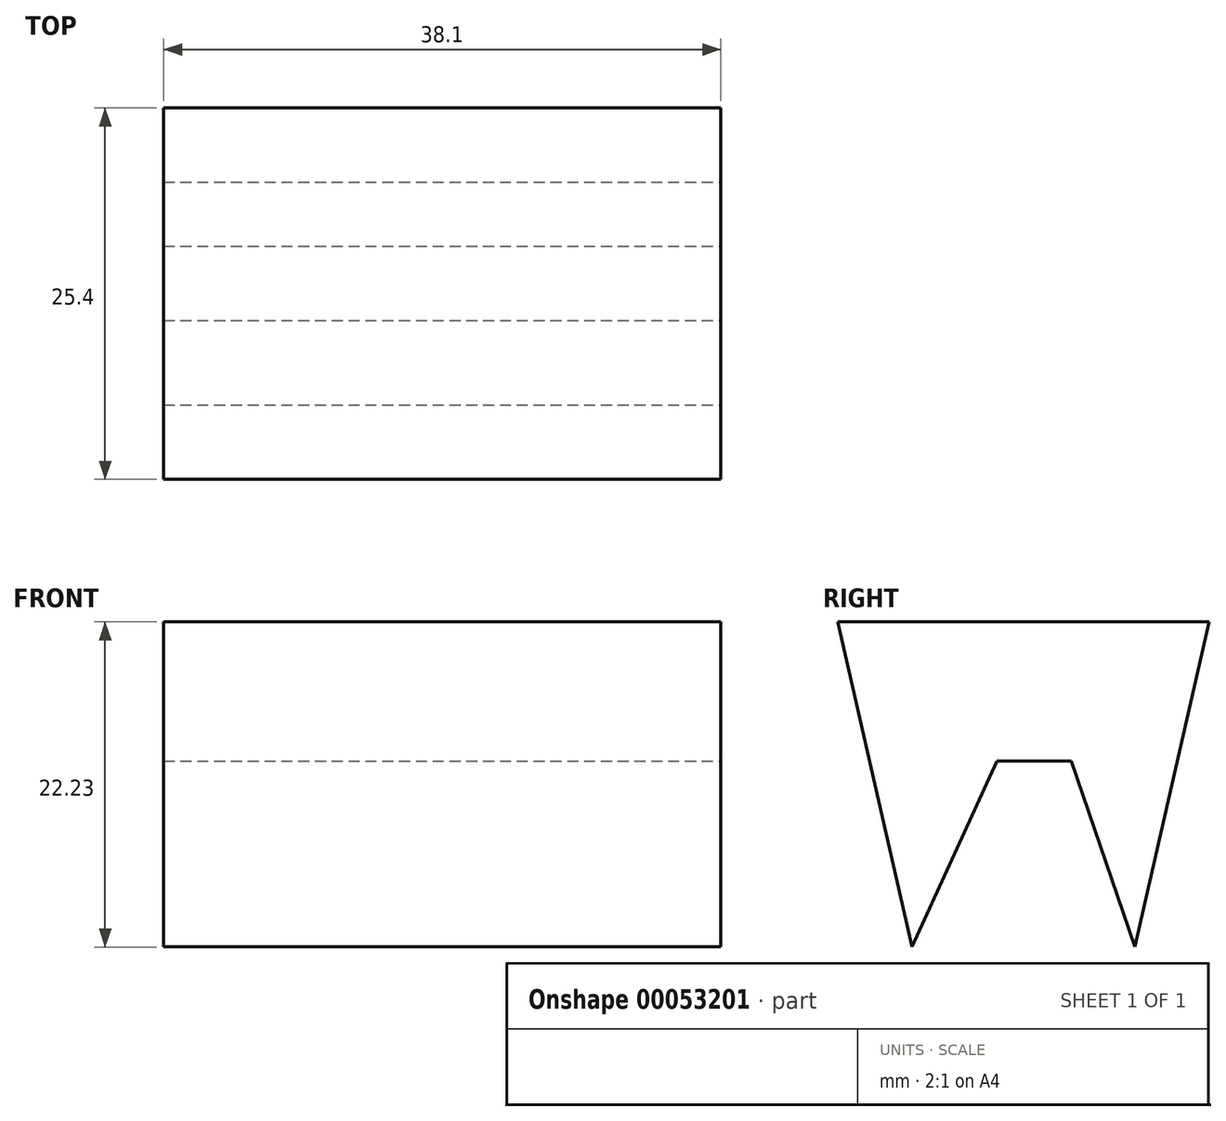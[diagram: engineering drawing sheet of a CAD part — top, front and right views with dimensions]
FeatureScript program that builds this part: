
annotation { "Feature Type Name" : "Feature", "Feature Type Description" : "" }
export const myFeature = defineFeature(function(context is Context, id is Id, definition is map)
    precondition{}
    {
        {
            var Q0;
            Q0=qCreatedBy(makeId("Front.planeOp"),FACE);
            var sketch = newSketch(context, id + "F0", { "sketchPlane" : qUnion([Q0])});
            skLineSegment(sketch, "E0.bottom", {"start": v(0, 0) * mm, "end": v(38.1, 0) * mm});
            skLineSegment(sketch, "E0.top", {"start": v(0, 38.1) * mm, "end": v(38.1, 38.1) * mm});
            skLineSegment(sketch, "E0.left", {"start": v(0, 0) * mm, "end": v(0, 38.1) * mm});
            skLineSegment(sketch, "E0.right", {"start": v(38.1, 0) * mm, "end": v(38.1, 38.1) * mm});
            skSolve(sketch);
        }
        {
            var Q0;
            Q0=makeQuery(id+"F0.imprint","IMPRINT",FACE,{"disambiguationData":[TD([[makeQuery(id+"F0.imprint","IMPRINT",EDGE,{"derivedFrom":sQuery(id+"F0.wireOp",EDGE,"E0.bottom")}),1.0]])]});
            extrude(context, id + "F1", {"entities" : qUnion([Q0]), "depth" : 38.1 * mm});
        }
        {
            var Q0;
            Q0=qCreatedBy(makeId("Front.planeOp"),FACE);
            cPlane(context, id + "F2", {"entities" : qUnion([Q0]), "cplaneType" : CPlaneType.OFFSET, "offset" : 38.1 * mm, "width" : 152.4 * mm, "height" : 152.4 * mm});
        }
        {
            var Q0;
            Q0=qCreatedBy(makeId("Right.planeOp"),FACE);
            cPlane(context, id + "F3", {"entities" : qUnion([Q0]), "cplaneType" : CPlaneType.OFFSET, "offset" : 38.1 * mm, "width" : 152.4 * mm, "height" : 152.4 * mm});
        }
        {
            var Q0;
            Q0=qCreatedBy(id+"F3.planeOp",FACE);
            var sketch = newSketch(context, id + "F4", { "sketchPlane" : qUnion([Q0])});
            skLineSegment(sketch, "E1", {"start": v(0, 0) * mm, "end": v(0, 38.1) * mm});
            skLineSegment(sketch, "E2", {"start": v(0, 38.1) * mm, "end": v(-38.1, 38.1) * mm});
            skLineSegment(sketch, "E3", {"start": v(-38.1, 38.1) * mm, "end": v(-38.1, 0) * mm});
            skLineSegment(sketch, "E4", {"start": v(-38.1, 38.1) * mm, "end": v(-31.75, 0) * mm});
            skLineSegment(sketch, "E5", {"start": v(-31.75, 0) * mm, "end": v(-25.4, 0) * mm});
            skLineSegment(sketch, "E6", {"start": v(-12.7, 0) * mm, "end": v(-6.35, 0) * mm});
            skLineSegment(sketch, "E7", {"start": v(-6.35, 0) * mm, "end": v(0, 38.1) * mm});
            skLineSegment(sketch, "E8", {"start": v(0, 38.1) * mm, "end": v(-6.35, 38.1) * mm});
            skLineSegment(sketch, "E9", {"start": v(-31.75, 38.1) * mm, "end": v(-38.1, 38.1) * mm});
            skLineSegment(sketch, "E10", {"start": v(-31.75, 38.1) * mm, "end": v(-26.67, 15.88) * mm});
            skLineSegment(sketch, "E11", {"start": v(-26.67, 15.88) * mm, "end": v(-20.87, 28.58) * mm});
            skLineSegment(sketch, "E12", {"start": v(-20.87, 28.58) * mm, "end": v(-15.8, 28.58) * mm});
            skLineSegment(sketch, "E13", {"start": v(-15.8, 28.58) * mm, "end": v(-11.43, 15.88) * mm});
            skLineSegment(sketch, "E14", {"start": v(-11.43, 15.87) * mm, "end": v(-6.35, 38.1) * mm});
            skLineSegment(sketch, "E15", {"start": v(-25.4, 0) * mm, "end": v(-19.05, 15.88) * mm});
            skLineSegment(sketch, "E16", {"start": v(-19.05, 15.88) * mm, "end": v(-12.7, 0) * mm});
            skLineSegment(sketch, "E17", {"start": v(-38.1, 0) * mm, "end": v(0, 0) * mm});
            skSolve(sketch);
        }
        {
            var Q0;
            Q0=makeQuery(id+"F4.imprint","IMPRINT",FACE,{"disambiguationData":[TD([[makeQuery(id+"F4.imprint","IMPRINT",EDGE,{"derivedFrom":sQuery(id+"F4.wireOp",EDGE,"E2")}),1.0]])]});
            var Q1;
            {var subQ0=sQuery(id+"F4.wireOp",EDGE,"E3");Q1=makeQuery(id+"F4.imprint","IMPRINT",FACE,{"disambiguationData":[TD([[makeQuery(id+"F4.imprint","IMPRINT",EDGE,{"derivedFrom":subQ0}),1.0]])]});}
            var Q2;
            {var subQ0=sQuery(id+"F4.wireOp",EDGE,"E15");Q2=makeQuery(id+"F4.imprint","IMPRINT",FACE,{"disambiguationData":[TD([[makeQuery(id+"F4.imprint","IMPRINT",EDGE,{"derivedFrom":subQ0}),-1.0]])]});}
            var Q3;
            {var subQ0=sQuery(id+"F4.wireOp",EDGE,"E1");Q3=makeQuery(id+"F4.imprint","IMPRINT",FACE,{"disambiguationData":[TD([[makeQuery(id+"F4.imprint","IMPRINT",EDGE,{"derivedFrom":subQ0}),1.0]])]});}
            extrude(context, id + "F5", {"entities" : qUnion([Q0, Q1, Q2, Q3]), "operationType" : NewBodyOperationType.REMOVE, "oppositeDirection" : true, "depth" : 38.1 * mm});
        }
    });
